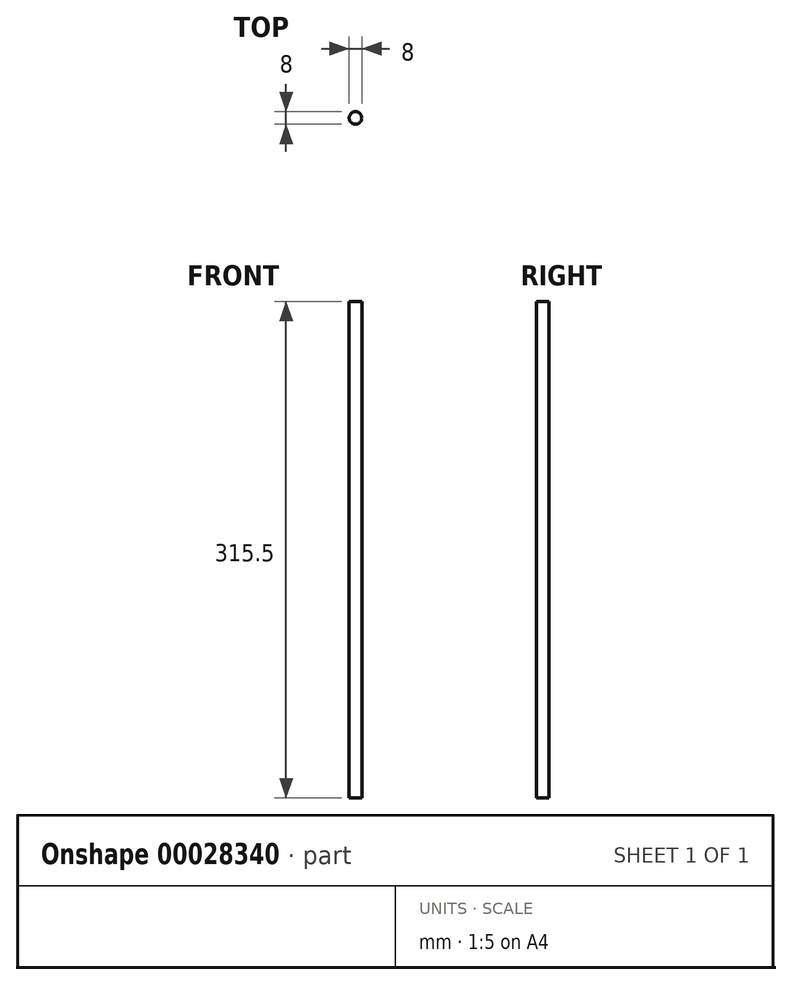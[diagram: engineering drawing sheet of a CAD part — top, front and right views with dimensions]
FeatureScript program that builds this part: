
annotation { "Feature Type Name" : "Feature", "Feature Type Description" : "" }
export const myFeature = defineFeature(function(context is Context, id is Id, definition is map)
    precondition{}
    {
        {
            var Q0;
            Q0=qCreatedBy(makeId("Top.planeOp"),FACE);
            var sketch = newSketch(context, id + "F0", { "sketchPlane" : qUnion([Q0])});
            skCircle(sketch, "E0", {"center": v(0, 0) * mm, "radius": 4 * mm});
            skSolve(sketch);
        }
        {
            var Q0;
            Q0=qSketchRegion(id+"F0",true);
            extrude(context, id + "F1", {"entities" : qUnion([Q0]), "depth" : 315.5 * mm});
        }
    });
